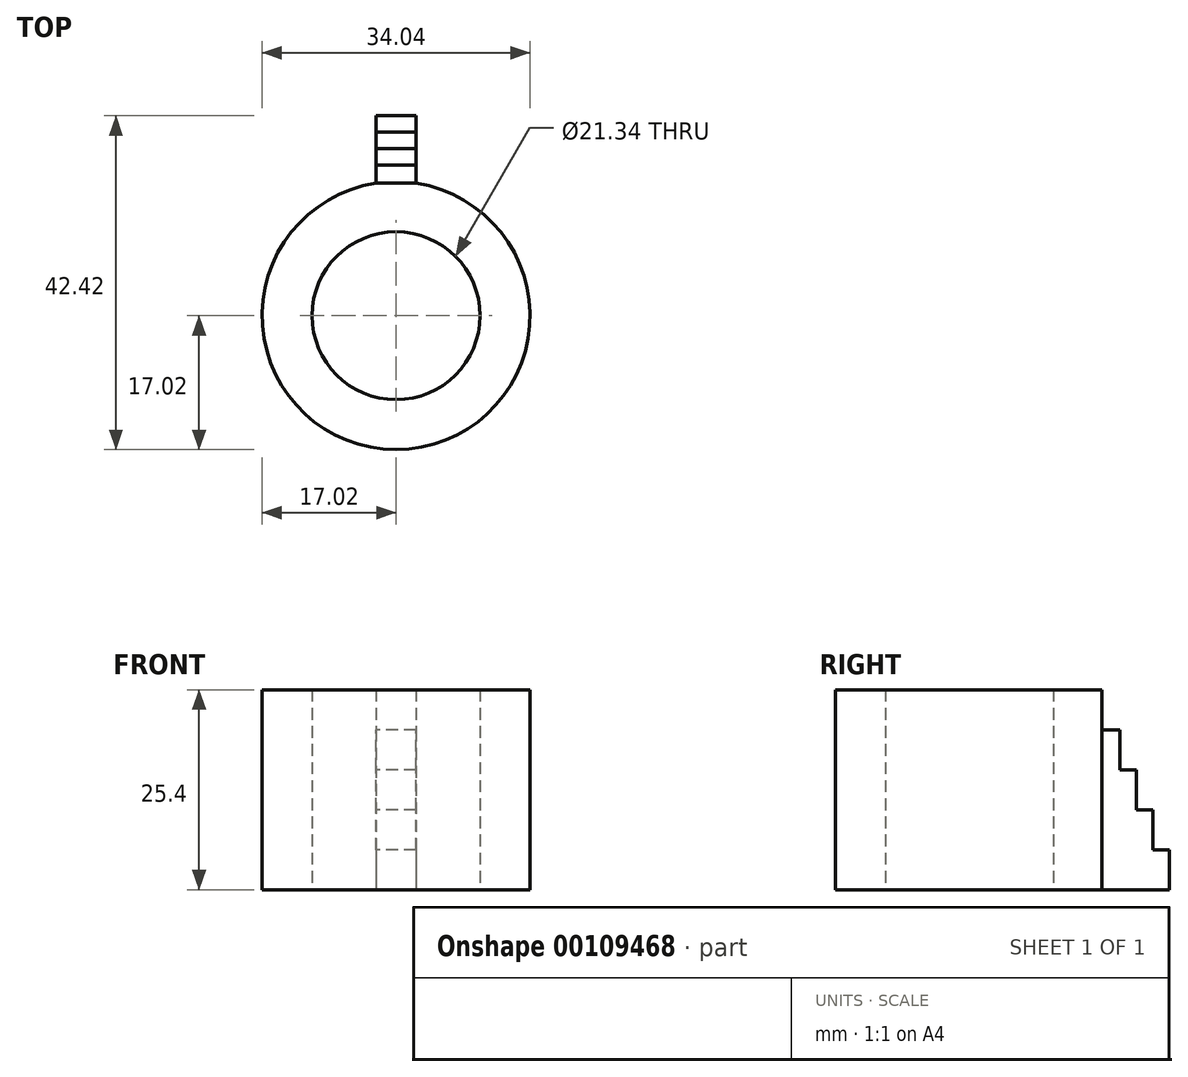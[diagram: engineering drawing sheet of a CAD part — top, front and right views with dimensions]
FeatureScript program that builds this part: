
annotation { "Feature Type Name" : "Feature", "Feature Type Description" : "" }
export const myFeature = defineFeature(function(context is Context, id is Id, definition is map)
    precondition{}
    {
        {
            var Q0;
            Q0=qCreatedBy(makeId("Top.planeOp"),FACE);
            var sketch = newSketch(context, id + "F0", { "sketchPlane" : qUnion([Q0])});
            skCircle(sketch, "E0", {"center": v(0, 0) * mm, "radius": 10.67 * mm});
            skArc(sketch, "E1", {"start": v(-2.54, 16.83) * mm, "mid": v(0, -17.02) * mm, "end": v(2.54, 16.83) * mm});
            skLineSegment(sketch, "E2.bottom", {"start": v(-2.54, 25.4) * mm, "end": v(2.54, 25.4) * mm});
            skLineSegment(sketch, "E2.left", {"start": v(-2.54, 25.4) * mm, "end": v(-2.54, 16.83) * mm});
            skLineSegment(sketch, "E2.right", {"start": v(2.54, 25.4) * mm, "end": v(2.54, 16.83) * mm});
            skSolve(sketch);
        }
        {
            var Q0;
            Q0=makeQuery(id+"F0.imprint","IMPRINT",FACE,{"disambiguationData":[TD([[makeQuery(id+"F0.imprint","IMPRINT",EDGE,{"derivedFrom":sQuery(id+"F0.wireOp",EDGE,"E0")}),-1.0]])]});
            extrude(context, id + "F1", {"entities" : qUnion([Q0]), "depth" : 25.4 * mm});
        }
        {
            var Q0;
            Q0=qCreatedBy(makeId("Right.planeOp"),FACE);
            var sketch = newSketch(context, id + "F2", { "sketchPlane" : qUnion([Q0])});
            skLineSegment(sketch, "E3.0", {"start": v(25.4, 5.08) * mm, "end": v(25.4, 0) * mm});
            skLineSegment(sketch, "E4", {"start": v(25.4, 0) * mm, "end": v(25.4, -8.08) * mm});
            skLineSegment(sketch, "E5", {"start": v(25.4, -8.08) * mm, "end": v(34.96, -8.08) * mm});
            skLineSegment(sketch, "E6", {"start": v(34.96, -8.08) * mm, "end": v(34.96, 29.4) * mm});
            skLineSegment(sketch, "E7", {"start": v(34.96, 29.4) * mm, "end": v(16.83, 29.4) * mm});
            skLineSegment(sketch, "E8", {"start": v(16.83, 20.32) * mm, "end": v(19.11, 20.32) * mm});
            skLineSegment(sketch, "E9", {"start": v(19.11, 20.32) * mm, "end": v(19.11, 15.24) * mm});
            skLineSegment(sketch, "E10", {"start": v(19.11, 15.24) * mm, "end": v(21.2, 15.24) * mm});
            skLineSegment(sketch, "E11", {"start": v(21.2, 15.24) * mm, "end": v(21.2, 10.16) * mm});
            skLineSegment(sketch, "E12", {"start": v(21.2, 10.16) * mm, "end": v(23.3, 10.16) * mm});
            skLineSegment(sketch, "E13", {"start": v(23.3, 10.16) * mm, "end": v(23.3, 5.08) * mm});
            skLineSegment(sketch, "E14", {"start": v(23.3, 5.08) * mm, "end": v(25.4, 5.08) * mm});
            skPoint(sketch, "E15.orphan", {"position": v(25.4, 25.4) * mm});
            skLineSegment(sketch, "E16.0", {"start": v(16.83, 29.4) * mm, "end": v(16.83, 20.32) * mm});
            skPoint(sketch, "E17.orphan", {"position": v(16.83, 25.4) * mm});
            skPoint(sketch, "E18.orphan", {"position": v(16.83, 0) * mm});
            skSolve(sketch);
        }
        {
            var Q0;
            Q0=makeQuery(id+"F2.imprint","IMPRINT",FACE,{"disambiguationData":[TD([[makeQuery(id+"F2.imprint","IMPRINT",EDGE,{"derivedFrom":sQuery(id+"F2.wireOp",EDGE,"E3.0")}),1.0]])]});
            extrude(context, id + "F3", {"entities" : qUnion([Q0]), "operationType" : NewBodyOperationType.REMOVE, "depth" : 25.4 * mm, "symmetric" : true});
        }
    });
